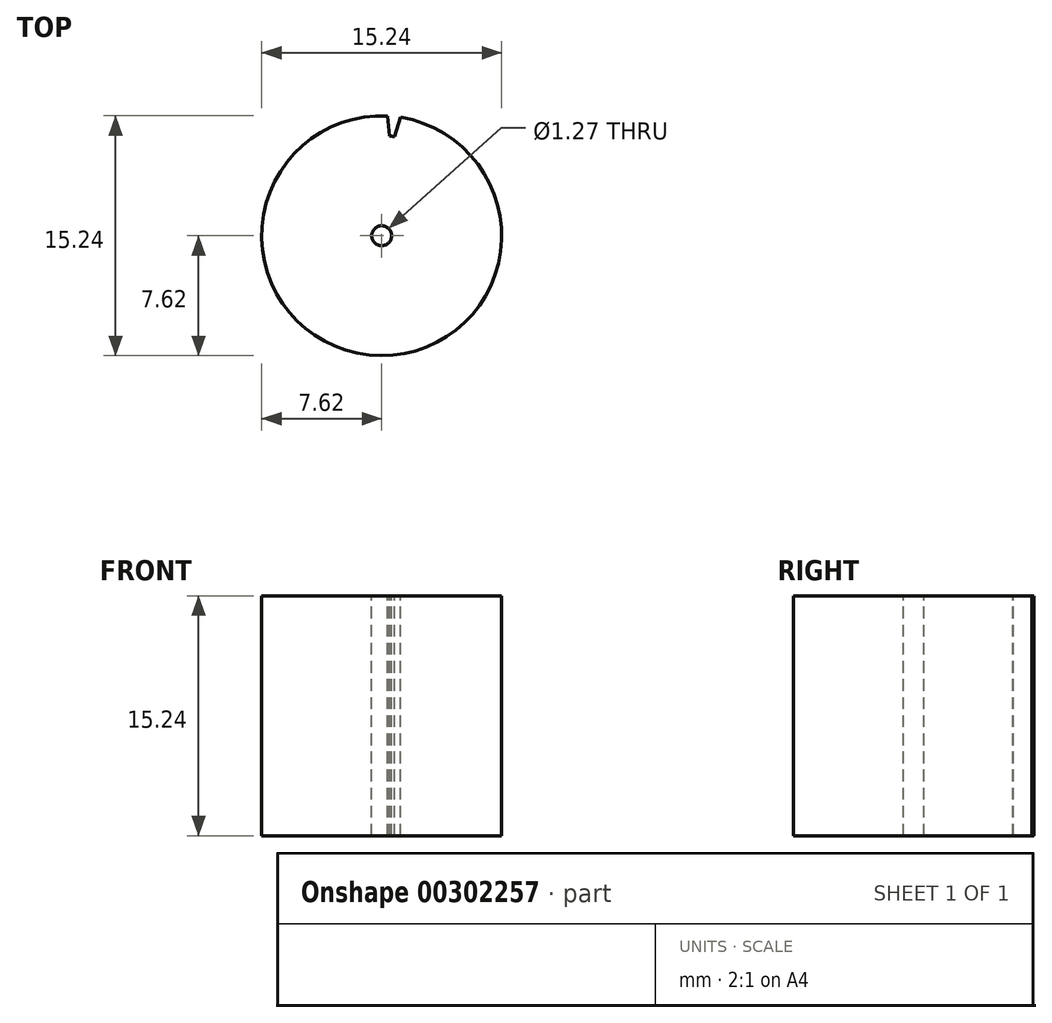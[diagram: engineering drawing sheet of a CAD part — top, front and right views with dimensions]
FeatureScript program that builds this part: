
annotation { "Feature Type Name" : "Feature", "Feature Type Description" : "" }
export const myFeature = defineFeature(function(context is Context, id is Id, definition is map)
    precondition{}
    {
        {
            var Q0;
            Q0=qCreatedBy(makeId("Top.planeOp"),FACE);
            var sketch = newSketch(context, id + "F0", { "sketchPlane" : qUnion([Q0])});
            skCircle(sketch, "E0", {"center": v(0, 0) * mm, "radius": 7.62 * mm});
            skSolve(sketch);
        }
        {
            var Q0;
            Q0 = qSketchRegion(id + "F0", true);
            extrude(context, id + "F1", {"entities" : qUnion([Q0]), "endBound" : BoundingType.SYMMETRIC, "depth" : 15.24 * mm});
        }
        {
            var Q0;
            Q0=makeQuery(id+"F1.opExtrude","CAP_FACE",FACE,{"disambiguationData":[OSD([sQuery(id+"F0.wireOp",EDGE,"E0")])],"isStart":false});
            var sketch = newSketch(context, id + "F2", { "sketchPlane" : qUnion([Q0])});
            skCircle(sketch, "E1", {"center": v(0, 0) * mm, "radius": 0.64 * mm});
            skSolve(sketch);
        }
        {
            var Q0;
            Q0 = qSketchRegion(id + "F2", true);
            var Q1;
            Q1=makeQuery(id+"F1.opExtrude","CAP_FACE",FACE,{"disambiguationData":[OSD([sQuery(id+"F0.wireOp",EDGE,"E0")])],"isStart":true});
            extrude(context, id + "F3", {"entities" : qUnion([Q0]), "operationType" : NewBodyOperationType.REMOVE, "endBound" : BoundingType.UP_TO_SURFACE, "oppositeDirection" : true, "endBoundEntityFace" : qUnion([Q1]), "depth" : 25.4 * mm});
        }
        {
            var Q0;
            Q0=makeQuery(id+"F1.opExtrude","CAP_FACE",FACE,{"disambiguationData":[OSD([sQuery(id+"F0.wireOp",EDGE,"E0")])],"isStart":false});
            var sketch = newSketch(context, id + "F4", { "sketchPlane" : qUnion([Q0])});
            skLineSegment(sketch, "E2", {"start": v(0, 11.33) * mm, "end": v(0, -11.37) * mm, "construction": true});
            skCircle(sketch, "E3", {"center": v(0, 0) * mm, "radius": 6.35 * mm, "construction": true});
            skLineSegment(sketch, "E4", {"start": v(-2.02, -9.52) * mm, "end": v(2.04, 9.62) * mm, "construction": true});
            skArc(sketch, "E5", {"start": v(0.38, 7.61) * mm, "mid": v(0.8, 7.58) * mm, "end": v(1.2, 7.52) * mm});
            skArc(sketch, "E6", {"start": v(0.5, 6.33) * mm, "mid": v(0.66, 6.32) * mm, "end": v(0.82, 6.3) * mm});
            skLineSegment(sketch, "E7", {"start": v(0.38, 7.61) * mm, "end": v(0.5, 6.33) * mm});
            skLineSegment(sketch, "E8", {"start": v(0.82, 6.3) * mm, "end": v(1.2, 7.52) * mm});
            skSolve(sketch);
        }
        {
            var Q0;
            Q0 = qSketchRegion(id + "F4", true);
            var Q1;
            Q1=makeQuery(id+"F1.opExtrude","CAP_FACE",FACE,{"disambiguationData":[OSD([sQuery(id+"F0.wireOp",EDGE,"E0")])],"isStart":true});
            extrude(context, id + "F5", {"entities" : qUnion([Q0]), "operationType" : NewBodyOperationType.REMOVE, "endBound" : BoundingType.UP_TO_SURFACE, "oppositeDirection" : true, "endBoundEntityFace" : qUnion([Q1]), "depth" : 25.4 * mm});
        }
        {
            var Q0;
            Q0=qCreatedBy(makeId("Right.planeOp"),FACE);
            var sketch = newSketch(context, id + "F6", { "sketchPlane" : qUnion([Q0])});
            skLineSegment(sketch, "E9", {"start": v(0, 23.96) * mm, "end": v(0, -23.77) * mm, "construction": true});
            skSolve(sketch);
        }
    });
